# Revit family: 3036975+3036930 Sylvania Lighting Fixture LUMISTRIP HO IP65 5M NW with LUMISTRIP ALU PROFILE OPAL 1M
name_source: partatom
category: Lighting Fixtures
revit_build: Autodesk Revit 2017 (Build: 20190507_1515(x64)
units: mm (PartAtom-declared; Revit-internal decimal feet)

## family parameters
Cut with Voids When Loaded = No
Host = Face
Light Source = Yes
OmniClass Number = 23.80.70.00
OmniClass Title = Lighting
Part Type = Normal
Room Calculation Point = No
Round Connector Dimension = Use Diameter
Shared = No

## types (1)
- 3036975+3036930 LUMISTRIP HO IP65 5M NW with LUMISTRIP ALU PROFILE OPAL 1M
    AccessoryMaterial = Body-Sylvania-Lumistrip-PC
    Apparent Load = 82 VA
    Assembly Code = D5020200
    AssetType = Fixed
    BodyFilletBottom_FEILO = 1 mm  [stored 0.00328084 ft]
    BodyFilletTop_FEILO = 1 mm  [stored 0.00328084 ft]
    BodyHeight_FEILO = 19 mm
    BodyLength_FEILO = 1000 mm  [stored 3.28084 ft]
    BodyMaterial = Body-Sylvania-Lumistrip-Aluminium
    BodyThickness_FEILO = 1 mm  [stored 0.00328084 ft]
    BodyWidth_FEILO = 25 mm  [stored 0.082021 ft]
    ClassificationName = Uniclass2015
    ClassificationValue = EF_70_80
    Color Filter = 16777215
    Cost = 0 $
    Default Elevation = 1219 mm
    DiffuserCutOff_FEILO = 8 mm  [stored 0.0262467 ft]
    DiffuserMaterial = Diffuser-Sylvania-Lumistrip-Transparent
    Dimming Lamp Color Temperature Shift = <None>
    DocumentationLiterature = http://www.sylvania-lighting.com
    DurationUnit = hours
    ElectricShockClassification = Class III
    Emit Shape Visible in Rendering = No
    Emit from Rectangle Length = 984 mm  [stored 3.22835 ft]
    Emit from Rectangle Width = 25 mm  [stored 0.082021 ft]
    EndCapOverhangL_FEILO = 6 mm  [stored 0.019685 ft]
    EndCapOverhangR_FEILO = -6 mm  [stored -0.019685 ft]
    ExpectedLife = 50000
    IfcExportAs = IfcLightFixtureType
    IfcExportType = IfcLightFixtureType
    IngressProtection = IP65
    InputVoltage = 24V DC
    Keynote = 16500
    Lamp = LED
    LampColourRenderingIndex = 80
    LampColourTemperature = 4000 K
    LampsType = LED
    LightOutputRatio = 100
    LuminousEfficacy = 85.60 lm/W
    Manufacturer = Feilo Sylvania
    ManufacturerName = Feilo Sylvania
    Material = silicon housing, silicon diffuser
    Model = LUMISTRIP HO IP65 5M NW with LUMISTRIP ALU PROFILE OPAL 1M
    ModelNumber = 3036975+3036930
    ModelReference = LUMISTRIP HO IP65 5M NW with LUMISTRIP ALU PROFILE OPAL 1M
    Name = LUMISTRIP HO IP65 5M NW with LUMISTRIP ALU PROFILE OPAL 1M
    NominalDepth = 14 mm  [stored 0.0459318 ft]
    NominalHeight = 4 mm  [stored 0.0131234 ft]
    NominalLength = 5000 mm
    Photometric Web File = 3036975.ies
    PowerFactor = 0
    ReflectorMaterial = <By Category>
    Tilt Angle = -90.00°
    Type Image = <None>
    TypeName = LUMISTRIP HO IP65 5M NW with LUMISTRIP ALU PROFILE OPAL 1M
    URL = http://www.sylvania-lighting.com
    Voltage = 24 V

note: [stored X ft] marks values corroborated as IEEE doubles in the binary element streams (Revit-internal decimal feet)

## geometry (parser evidence)
native form markers: Sweep x1
no freeform markers — native parametric forms only
